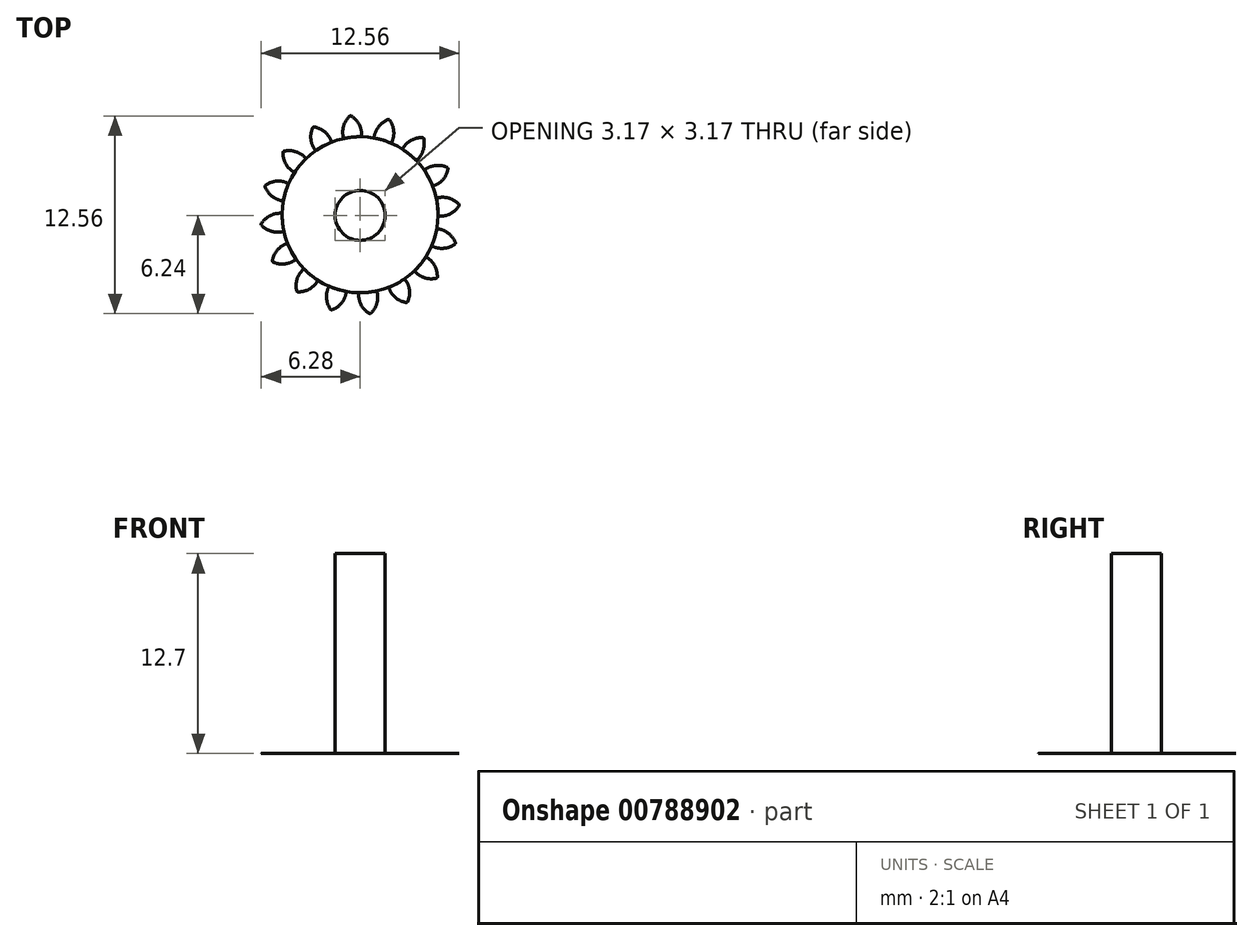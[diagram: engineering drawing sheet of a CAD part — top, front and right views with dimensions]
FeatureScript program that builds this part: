
annotation { "Feature Type Name" : "Feature", "Feature Type Description" : "" }
export const myFeature = defineFeature(function(context is Context, id is Id, definition is map)
    precondition{}
    {
        {
            var Q0;
            Q0=qCreatedBy(makeId("Top.planeOp"),FACE);
            var sketch = newSketch(context, id + "F0", { "sketchPlane" : qUnion([Q0])});
            skCircle(sketch, "E0", {"center": v(0, 0) * mm, "radius": 6.35 * mm, "construction": true});
            skCircle(sketch, "E1", {"center": v(0, 0.04) * mm, "radius": 5.59 * mm, "construction": true});
            skCircle(sketch, "E2", {"center": v(0, 0.04) * mm, "radius": 4.95 * mm});
            skLineSegment(sketch, "E3", {"start": v(0, 0.04) * mm, "end": v(0, 7.06) * mm, "construction": true});
            skLineSegment(sketch, "E4", {"start": v(0, 5.63) * mm, "end": v(-6.1, 5.63) * mm, "construction": true});
            skLineSegment(sketch, "E5", {"start": v(0, 0.04) * mm, "end": v(-0.72, 7.35) * mm, "construction": true});
            skLineSegment(sketch, "E6", {"start": v(0, 5.63) * mm, "end": v(-5.91, 3.48) * mm, "construction": true});
            skCircle(sketch, "E7", {"center": v(0, 0.04) * mm, "radius": 5.25 * mm, "construction": true});
            skCircle(sketch, "E8", {"center": v(0, 5.63) * mm, "radius": 1.4 * mm, "construction": true});
            skCircle(sketch, "E9", {"center": v(-1.3, 5.13) * mm, "radius": 1.4 * mm, "construction": true});
            skArc(sketch, "E10", {"start": v(0, 5.63) * mm, "mid": v(-0.23, 6.02) * mm, "end": v(-0.58, 6.32) * mm});
            skArc(sketch, "E11", {"start": v(0.09, 5) * mm, "mid": v(0.08, 5.32) * mm, "end": v(0, 5.63) * mm});
            skArc(sketch, "E12.MirrorCS", {"start": v(-1.1, 5.52) * mm, "mid": v(-0.94, 5.95) * mm, "end": v(-0.65, 6.32) * mm});
            skArc(sketch, "E13.MirrorCS", {"start": v(-1.05, 4.88) * mm, "mid": v(-1.1, 5.2) * mm, "end": v(-1.1, 5.52) * mm});
            skArc(sketch, "E14", {"start": v(-0.58, 6.32) * mm, "mid": v(-0.62, 6.32) * mm, "end": v(-0.65, 6.32) * mm});
            skCircle(sketch, "E15", {"center": v(0, 0) * mm, "radius": 1.59 * mm});
            skSolve(sketch);
        }
        {
            var Q0;
            Q0=makeQuery(id+"F0.imprint","IMPRINT",FACE,{"disambiguationData":[TD([[makeQuery(id+"F0.imprint","IMPRINT",EDGE,{"derivedFrom":sQuery(id+"F0.wireOp",EDGE,"E10")}),1.0]])]});
            extrude(context, id + "F1", {"entities" : qUnion([Q0]), "depth" : 1 / 406.4 * mm, "offsetDistance" : 25.4 * mm});
        }
        {
            var Q0;
            Q0=makeQuery(id+"F1.opExtrude","SWEPT_BODY",BODY,{"disambiguationData":[OSD([sQuery(id+"F0.wireOp",EDGE,"E2"),sQuery(id+"F0.wireOp",EDGE,"E10"),sQuery(id+"F0.wireOp",EDGE,"E11"),sQuery(id+"F0.wireOp",EDGE,"E12.MirrorCS"),sQuery(id+"F0.wireOp",EDGE,"E13.MirrorCS"),sQuery(id+"F0.wireOp",EDGE,"E14")])]});
            var Q1;
            Q1=sQuery(id+"F0.wireOp",EDGE,"E2");
            circularPattern(context, id + "F2", {"entities" : qUnion([Q0]), "axis" : qUnion([Q1]), "angle" : 360 * degree, "instanceCount" : 16, "equalSpace" : true});
        }
        {
            var Q0;
            Q0=makeQuery(id+"F0.imprint","IMPRINT",FACE,{"disambiguationData":[TD([[makeQuery(id+"F0.imprint","IMPRINT",EDGE,{"derivedFrom":sQuery(id+"F0.wireOp",EDGE,"E15")}),-1.0]])]});
            extrude(context, id + "F3", {"entities" : qUnion([Q0]), "depth" : 1 / 406.4 * mm, "offsetDistance" : 25.4 * mm});
        }
        {
            var Q0;
            Q0=makeQuery(id+"F0.imprint","IMPRINT",FACE,{"disambiguationData":[TD([[makeQuery(id+"F0.imprint","IMPRINT",EDGE,{"derivedFrom":sQuery(id+"F0.wireOp",EDGE,"E15")}),1.0]])]});
            extrude(context, id + "F4", {"entities" : qUnion([Q0]), "operationType" : NewBodyOperationType.ADD, "depth" : 12.7 * mm, "offsetDistance" : 25.4 * mm});
        }
    });
